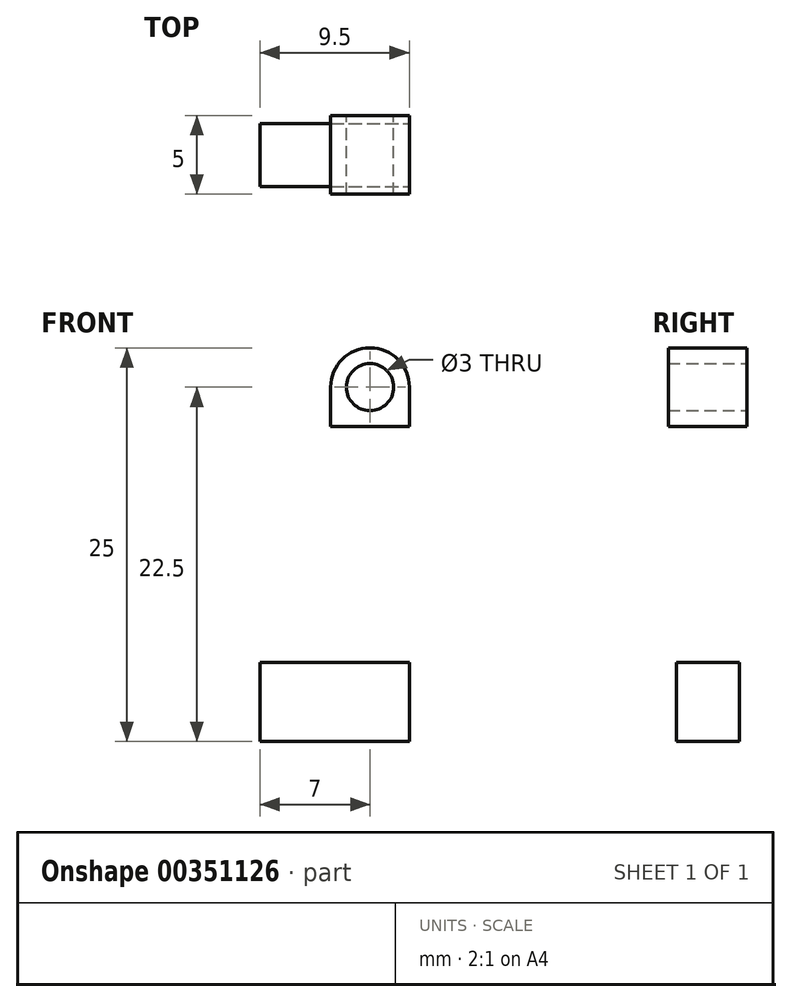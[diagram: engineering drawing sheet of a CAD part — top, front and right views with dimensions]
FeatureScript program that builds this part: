
annotation { "Feature Type Name" : "Feature", "Feature Type Description" : "" }
export const myFeature = defineFeature(function(context is Context, id is Id, definition is map)
    precondition{}
    {
        {
            var Q0;
            Q0=qCreatedBy(makeId("Front.planeOp"),FACE);
            var sketch = newSketch(context, id + "F0", { "sketchPlane" : qUnion([Q0])});
            skLineSegment(sketch, "E0.bottom", {"start": v(0, 0) * mm, "end": v(9.8, 0) * mm});
            skLineSegment(sketch, "E0.top", {"start": v(0, 5) * mm, "end": v(9.8, 5) * mm});
            skLineSegment(sketch, "E0.left", {"start": v(0, 0) * mm, "end": v(0, 5) * mm});
            skLineSegment(sketch, "E0.right", {"start": v(9.8, 0) * mm, "end": v(9.8, 5) * mm});
            skLineSegment(sketch, "E1.bottom", {"start": v(9.8, 5) * mm, "end": v(4.8, 5) * mm});
            skLineSegment(sketch, "E1.top", {"start": v(9.8, 20) * mm, "end": v(4.8, 20) * mm});
            skLineSegment(sketch, "E1.left", {"start": v(9.8, 5) * mm, "end": v(9.8, 20) * mm});
            skLineSegment(sketch, "E1.right", {"start": v(4.8, 5) * mm, "end": v(4.8, 20) * mm});
            skLineSegment(sketch, "E2", {"start": v(7.3, 5) * mm, "end": v(7.3, 25) * mm, "construction": true});
            skLineSegment(sketch, "E3", {"start": v(9.8, 5) * mm, "end": v(9.8, 15) * mm});
            skLineSegment(sketch, "E4", {"start": v(4.8, 20) * mm, "end": v(4.8, 25) * mm});
            skLineSegment(sketch, "E5", {"start": v(4.8, 25) * mm, "end": v(9.8, 25) * mm});
            skLineSegment(sketch, "E6", {"start": v(9.8, 25) * mm, "end": v(9.8, 20) * mm});
            skPoint(sketch, "E7.orphan", {"position": v(7.3, 20) * mm});
            skLineSegment(sketch, "E8", {"start": v(4.8, 22.5) * mm, "end": v(9.8, 22.5) * mm, "construction": true});
            skPoint(sketch, "E9", {"position": v(7.3, 22.5) * mm});
            skSolve(sketch);
        }
        {
            var Q0;
            Q0=makeQuery(id+"F0.imprint","IMPRINT",FACE,{"disambiguationData":[TD([[makeQuery(id+"F0.imprint","IMPRINT",EDGE,{"derivedFrom":sQuery(id+"F0.wireOp",EDGE,"E1.bottom")}),-1.0]])]});
            var Q1;
            Q1=makeQuery(id+"F0.imprint","IMPRINT",FACE,{"disambiguationData":[TD([[makeQuery(id+"F0.imprint","IMPRINT",EDGE,{"derivedFrom":sQuery(id+"F0.wireOp",EDGE,"E1.top")}),-1.0]])]});
            extrude(context, id + "F1", {"entities" : qUnion([Q0, Q1]), "depth" : 5 * mm});
        }
        {
            var Q0;
            Q0=sQuery(id+"F0.wireOp",VERTEX,"E9");
            var Q1;
            Q1=makeQuery(id+"F1.opExtrude","SWEPT_BODY",BODY,{"disambiguationData":[OSD([sQuery(id+"F0.wireOp",EDGE,"E0.bottom"),sQuery(id+"F0.wireOp",EDGE,"E0.top"),sQuery(id+"F0.wireOp",EDGE,"E0.left"),sQuery(id+"F0.wireOp",EDGE,"E0.right"),sQuery(id+"F0.wireOp",EDGE,"E1.left"),sQuery(id+"F0.wireOp",EDGE,"E1.right"),sQuery(id+"F0.wireOp",EDGE,"E3"),sQuery(id+"F0.wireOp",EDGE,"E4"),sQuery(id+"F0.wireOp",EDGE,"E5"),sQuery(id+"F0.wireOp",EDGE,"E6")])]});
            hole(context, id + "F2", {"style" : HoleStyle.SIMPLE, "endStyle" : HoleEndStyle.THROUGH, "oppositeDirection" : true, "holeDiameter" : 3 * mm, "isTappedThrough" : true, "tappedDepth" : 12 * mm, "tapClearance" : 3, "locations" : qUnion([Q0]), "scope" : qUnion([Q1])});
        }
        {
            var Q0;
            Q0=makeQuery(id+"F1.opExtrude","SWEPT_EDGE",EDGE,{"disambiguationData":[OSD([sQuery(id+"F0.wireOp",EDGE,"E4"),sQuery(id+"F0.wireOp",EDGE,"E5")])]});
            var Q1;
            Q1=makeQuery(id+"F1.opExtrude","SWEPT_EDGE",EDGE,{"disambiguationData":[OSD([sQuery(id+"F0.wireOp",EDGE,"E5"),sQuery(id+"F0.wireOp",EDGE,"E6")])]});
            fillet(context, id + "F3", {"entities" : qUnion([Q0, Q1]), "radius" : 2.5 * mm, "tangentPropagation" : true, "allowEdgeOverflow" : false});
        }
        {
            var Q0;
            Q0=makeQuery(id+"F1.opExtrude","SWEPT_FACE",FACE,{"disambiguationData":[OSD([sQuery(id+"F0.wireOp",EDGE,"E1.left"),sQuery(id+"F0.wireOp",EDGE,"E3"),sQuery(id+"F0.wireOp",EDGE,"E6")])]});
            var sketch = newSketch(context, id + "F4", { "sketchPlane" : qUnion([Q0])});
            skLineSegment(sketch, "E10", {"start": v(-2.5, 5) * mm, "end": v(-2.5, 0) * mm, "construction": true});
            skLineSegment(sketch, "E11", {"start": v(-5, 5) * mm, "end": v(0, 5) * mm});
            skLineSegment(sketch, "E12", {"start": v(-5, 5) * mm, "end": v(-4.9, 5) * mm});
            skLineSegment(sketch, "E13", {"start": v(0, 5) * mm, "end": v(-0.5, 5) * mm, "construction": true});
            skLineSegment(sketch, "E14", {"start": v(-0.5, 5) * mm, "end": v(-0.5, 0) * mm});
            skLineSegment(sketch, "E15", {"start": v(-0.5, 0) * mm, "end": v(-4.5, 0) * mm});
            skLineSegment(sketch, "E16", {"start": v(-5, 5) * mm, "end": v(-4.5, 5) * mm, "construction": true});
            skLineSegment(sketch, "E17", {"start": v(-4.5, 5) * mm, "end": v(-4.5, 0) * mm});
            skLineSegment(sketch, "E18", {"start": v(-4.5, 0) * mm, "end": v(-0.5, 0) * mm});
            skSolve(sketch);
        }
        {
            var Q0;
            Q0 = qSketchRegion(id + "F4", true);
            extrude(context, id + "F5", {"entities" : qUnion([Q0]), "operationType" : NewBodyOperationType.ADD, "depth" : -9.5 * mm});
        }
    });
